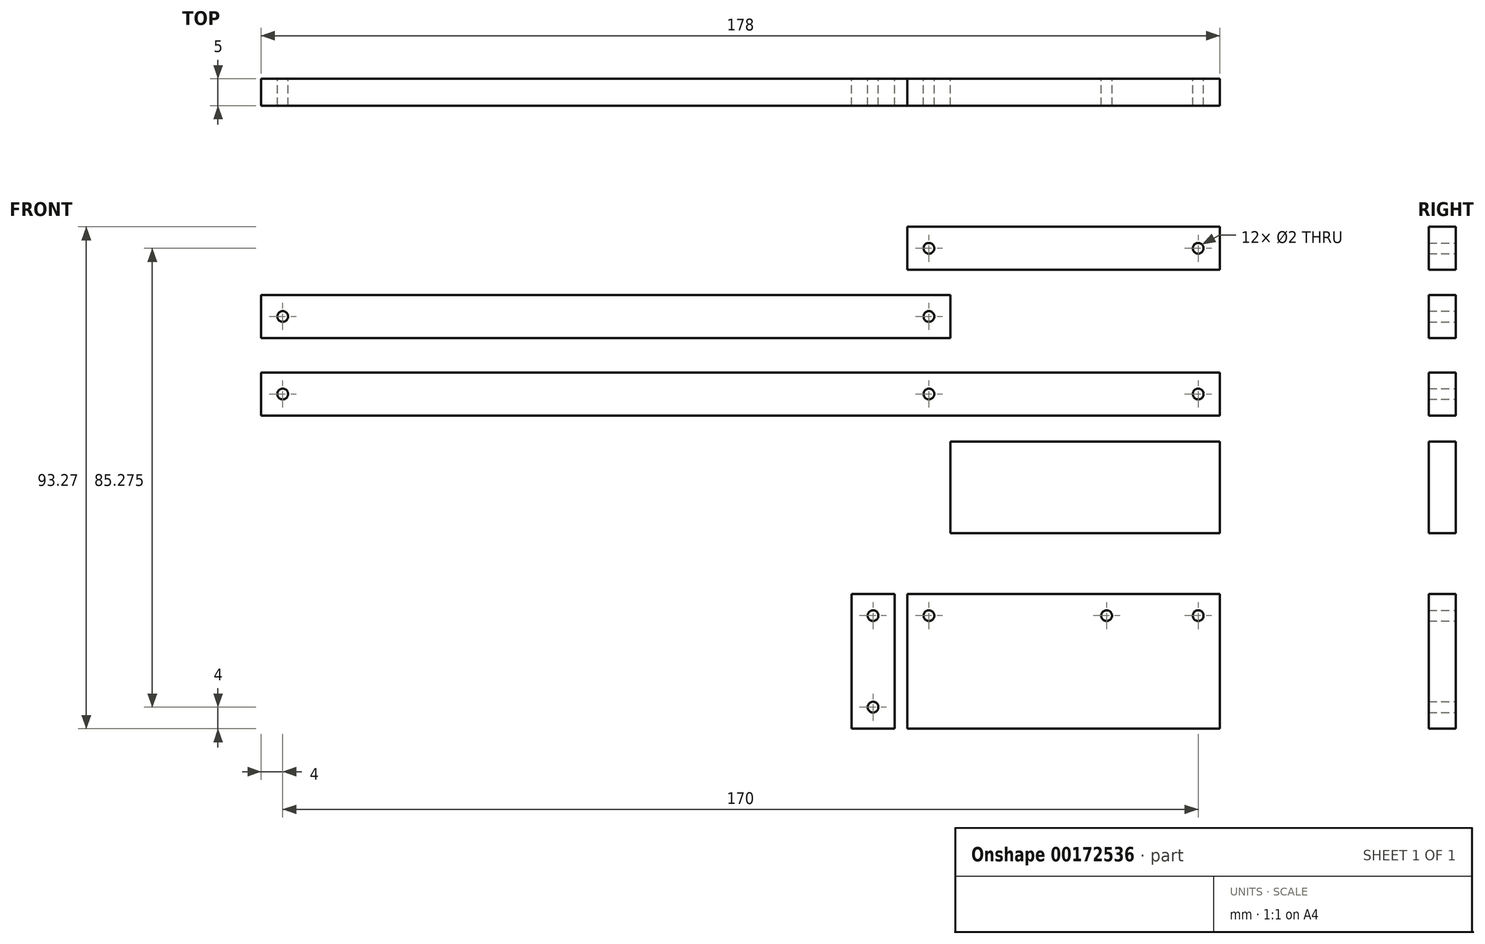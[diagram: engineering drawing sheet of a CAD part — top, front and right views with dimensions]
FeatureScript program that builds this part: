
annotation { "Feature Type Name" : "Feature", "Feature Type Description" : "" }
export const myFeature = defineFeature(function(context is Context, id is Id, definition is map)
    precondition{}
    {
        {
            var Q0;
            Q0=qCreatedBy(makeId("Front.planeOp"),FACE);
            var sketch = newSketch(context, id + "F0", { "sketchPlane" : qUnion([Q0])});
            skLineSegment(sketch, "E0", {"start": v(0, -14.8) * mm, "end": v(0, 98.5) * mm, "construction": true});
            skLineSegment(sketch, "E1", {"start": v(-120, 98.5) * mm, "end": v(-120, -14.8) * mm, "construction": true});
            skLineSegment(sketch, "E2", {"start": v(50, 98.5) * mm, "end": v(50, -14.8) * mm, "construction": true});
            skLineSegment(sketch, "E3.bottom", {"start": v(-124, 55.6) * mm, "end": v(4, 55.6) * mm});
            skLineSegment(sketch, "E3.top", {"start": v(-124, 47.6) * mm, "end": v(4, 47.6) * mm});
            skLineSegment(sketch, "E3.left", {"start": v(-124, 55.6) * mm, "end": v(-124, 47.6) * mm});
            skLineSegment(sketch, "E3.right", {"start": v(4, 55.6) * mm, "end": v(4, 47.6) * mm});
            skLineSegment(sketch, "E4.bottom", {"start": v(-124, 41.2) * mm, "end": v(54, 41.2) * mm});
            skLineSegment(sketch, "E4.top", {"start": v(-124, 33.2) * mm, "end": v(54, 33.2) * mm});
            skLineSegment(sketch, "E4.left", {"start": v(-124, 41.2) * mm, "end": v(-124, 33.2) * mm});
            skLineSegment(sketch, "E4.right", {"start": v(54, 41.2) * mm, "end": v(54, 33.2) * mm});
            skCircle(sketch, "E5", {"center": v(-120, 51.6) * mm, "radius": 1 * mm});
            skPoint(sketch, "E5.centerSnap0", {"position": v(-124, 51.6) * mm});
            skCircle(sketch, "E6", {"center": v(-120, 37.2) * mm, "radius": 1 * mm});
            skPoint(sketch, "E6.centerSnap0", {"position": v(-124, 37.2) * mm});
            skCircle(sketch, "E7", {"center": v(0, 51.6) * mm, "radius": 1 * mm});
            skPoint(sketch, "E7.centerSnap0", {"position": v(4, 51.6) * mm});
            skCircle(sketch, "E8", {"center": v(0, 37.2) * mm, "radius": 1 * mm});
            skPoint(sketch, "E8.centerSnap0", {"position": v(54, 37.2) * mm});
            skCircle(sketch, "E9", {"center": v(50, 37.2) * mm, "radius": 1 * mm});
            skLineSegment(sketch, "E10.bottom", {"start": v(-4, 28.33) * mm, "end": v(54, 28.33) * mm});
            skLineSegment(sketch, "E10.top", {"start": v(-4, 3.33) * mm, "end": v(54, 3.33) * mm});
            skLineSegment(sketch, "E10.left", {"start": v(-4, 28.33) * mm, "end": v(-4, 3.33) * mm});
            skLineSegment(sketch, "E10.right", {"start": v(54, 28.33) * mm, "end": v(54, 3.33) * mm});
            skLineSegment(sketch, "E11.bottom", {"start": v(54, 28.33) * mm, "end": v(4, 28.33) * mm});
            skLineSegment(sketch, "E11.top", {"start": v(54, 11.33) * mm, "end": v(4, 11.33) * mm});
            skLineSegment(sketch, "E11.left", {"start": v(54, 28.33) * mm, "end": v(54, 11.33) * mm});
            skLineSegment(sketch, "E11.right", {"start": v(4, 28.33) * mm, "end": v(4, 11.33) * mm});
            skCircle(sketch, "E12", {"center": v(0, 24.33) * mm, "radius": 1 * mm});
            skCircle(sketch, "E13", {"center": v(0, 7.33) * mm, "radius": 1 * mm});
            skCircle(sketch, "E14", {"center": v(50, 7.33) * mm, "radius": 1 * mm});
            skLineSegment(sketch, "E15.bottom", {"start": v(-4, 68.27) * mm, "end": v(54, 68.27) * mm});
            skLineSegment(sketch, "E15.top", {"start": v(-4, 60.27) * mm, "end": v(54, 60.27) * mm});
            skLineSegment(sketch, "E15.left", {"start": v(-4, 68.27) * mm, "end": v(-4, 60.27) * mm});
            skLineSegment(sketch, "E15.right", {"start": v(54, 68.27) * mm, "end": v(54, 60.27) * mm});
            skCircle(sketch, "E16", {"center": v(0, 64.27) * mm, "radius": 1 * mm});
            skPoint(sketch, "E16.centerSnap0", {"position": v(-4, 64.27) * mm});
            skCircle(sketch, "E17", {"center": v(50, 64.27) * mm, "radius": 1 * mm});
            skPoint(sketch, "E17.centerSnap0", {"position": v(54, 64.27) * mm});
            skLineSegment(sketch, "E18.bottom", {"start": v(-4, 0) * mm, "end": v(54, 0) * mm});
            skLineSegment(sketch, "E18.top", {"start": v(-4, -25) * mm, "end": v(54, -25) * mm});
            skLineSegment(sketch, "E18.left", {"start": v(-4, 0) * mm, "end": v(-4, -25) * mm});
            skLineSegment(sketch, "E18.right", {"start": v(54, 0) * mm, "end": v(54, -25) * mm});
            skLineSegment(sketch, "E19.bottom", {"start": v(-14.38, 0) * mm, "end": v(-6.38, 0) * mm});
            skLineSegment(sketch, "E19.top", {"start": v(-14.38, -25) * mm, "end": v(-6.38, -25) * mm});
            skLineSegment(sketch, "E19.left", {"start": v(-14.38, 0) * mm, "end": v(-14.38, -25) * mm});
            skLineSegment(sketch, "E19.right", {"start": v(-6.38, 0) * mm, "end": v(-6.38, -25) * mm});
            skCircle(sketch, "E20", {"center": v(0, -4) * mm, "radius": 1 * mm});
            skCircle(sketch, "E21", {"center": v(50, -4) * mm, "radius": 1 * mm});
            skCircle(sketch, "E22", {"center": v(-10.38, -4) * mm, "radius": 1 * mm});
            skPoint(sketch, "E22.centerSnap0", {"position": v(-10.38, 0) * mm});
            skCircle(sketch, "E23", {"center": v(-10.38, -21) * mm, "radius": 1 * mm});
            skPoint(sketch, "E23.centerSnap0", {"position": v(-10.38, -25) * mm});
            skCircle(sketch, "E24", {"center": v(33, -4) * mm, "radius": 1 * mm});
            skSolve(sketch);
        }
        {
            var Q0;
            Q0=makeQuery(id+"F0.imprint","IMPRINT",FACE,{"disambiguationData":[TD([[makeQuery(id+"F0.imprint","IMPRINT",EDGE,{"derivedFrom":sQuery(id+"F0.wireOp",EDGE,"E15.bottom")}),-1.0]])]});
            var Q1;
            Q1=makeQuery(id+"F0.imprint","IMPRINT",FACE,{"disambiguationData":[TD([[makeQuery(id+"F0.imprint","IMPRINT",EDGE,{"derivedFrom":sQuery(id+"F0.wireOp",EDGE,"E3.bottom")}),-1.0]])]});
            var Q2;
            Q2=makeQuery(id+"F0.imprint","IMPRINT",FACE,{"disambiguationData":[TD([[makeQuery(id+"F0.imprint","IMPRINT",EDGE,{"derivedFrom":sQuery(id+"F0.wireOp",EDGE,"E4.bottom")}),-1.0]])]});
            var Q3;
            Q3=makeQuery(id+"F0.imprint","IMPRINT",FACE,{"disambiguationData":[TD([[makeQuery(id+"F0.imprint","IMPRINT",EDGE,{"derivedFrom":sQuery(id+"F0.wireOp",EDGE,"E10.bottom")}),-1.0]])]});
            var Q4;
            Q4=makeQuery(id+"F0.imprint","IMPRINT",FACE,{"disambiguationData":[TD([[makeQuery(id+"F0.imprint","IMPRINT",EDGE,{"derivedFrom":sQuery(id+"F0.wireOp",EDGE,"E19.bottom")}),-1.0]])]});
            var Q5;
            Q5=makeQuery(id+"F0.imprint","IMPRINT",FACE,{"disambiguationData":[TD([[makeQuery(id+"F0.imprint","IMPRINT",EDGE,{"derivedFrom":sQuery(id+"F0.wireOp",EDGE,"E18.bottom")}),-1.0]])]});
            extrude(context, id + "F1", {"entities" : qUnion([Q0, Q1, Q2, Q3, Q4, Q5]), "depth" : 5 * mm});
        }
    });
